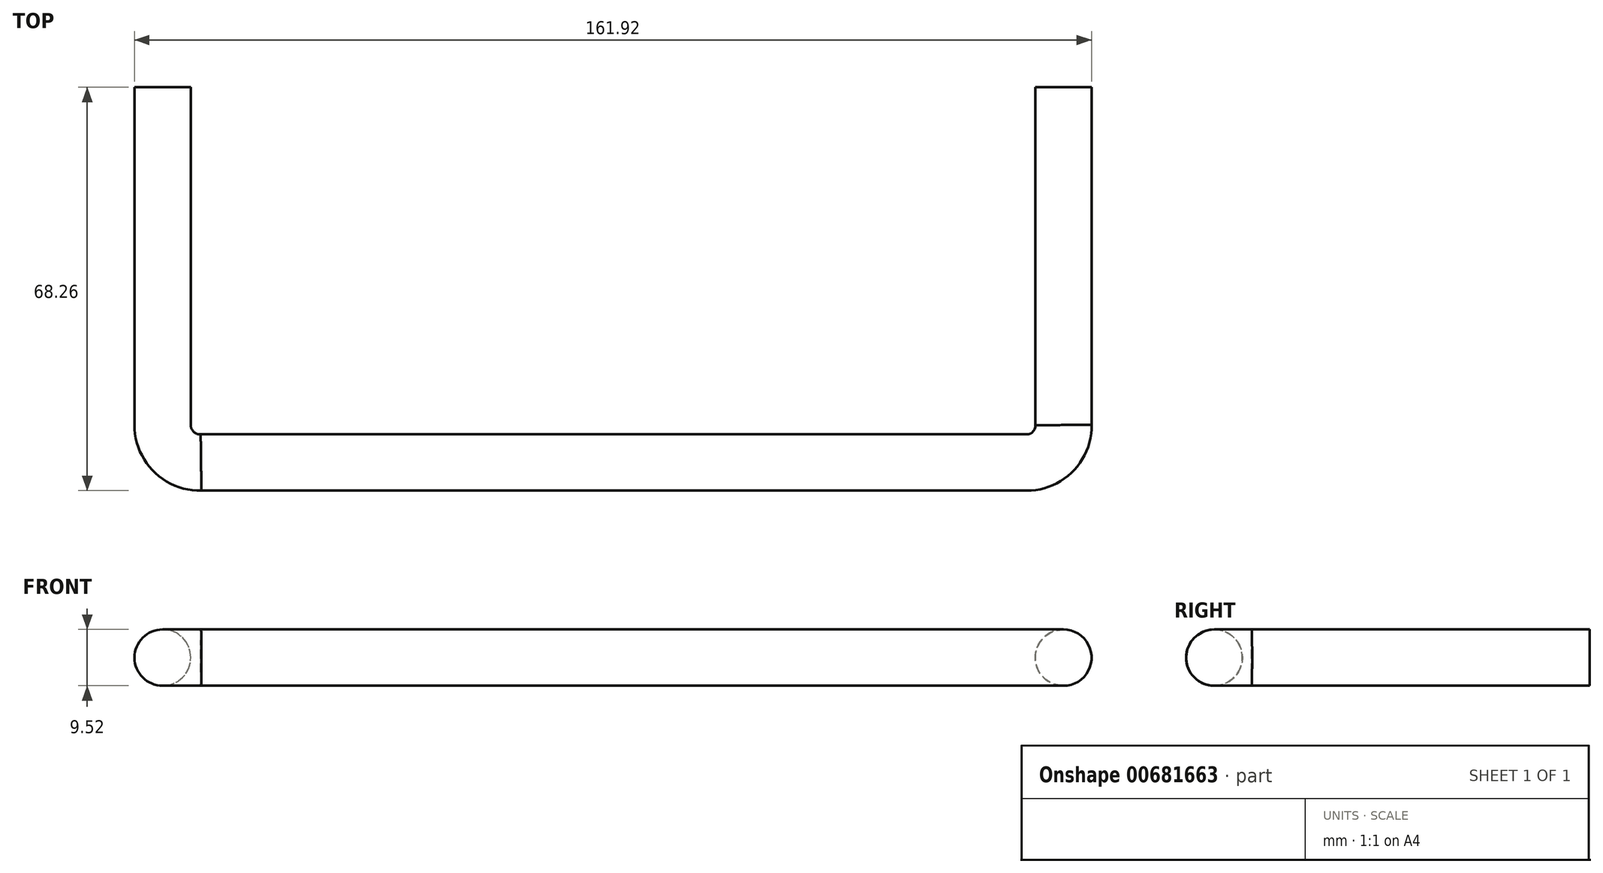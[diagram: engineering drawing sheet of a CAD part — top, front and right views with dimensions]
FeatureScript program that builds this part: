
annotation { "Feature Type Name" : "Feature", "Feature Type Description" : "" }
export const myFeature = defineFeature(function(context is Context, id is Id, definition is map)
    precondition{}
    {
        {
            var Q0;
            Q0=qCreatedBy(makeId("Front.planeOp"),FACE);
            var sketch = newSketch(context, id + "F0", { "sketchPlane" : qUnion([Q0])});
            skCircle(sketch, "E0", {"center": v(0, 0) * mm, "radius": 4.76 * mm});
            skSolve(sketch);
        }
        {
            var Q0;
            Q0=qCreatedBy(makeId("Top.planeOp"),FACE);
            var sketch = newSketch(context, id + "F1", { "sketchPlane" : qUnion([Q0])});
            skLineSegment(sketch, "E1", {"start": v(0, 0) * mm, "end": v(0, -57.15) * mm});
            skLineSegment(sketch, "E2", {"start": v(152.4, -57.15) * mm, "end": v(152.4, 0) * mm});
            skArc(sketch, "E3", {"start": v(0, -57.15) * mm, "mid": v(1.92, -61.7) * mm, "end": v(6.5, -63.5) * mm});
            skLineSegment(sketch, "E4", {"start": v(6.5, -63.5) * mm, "end": v(146.2, -63.5) * mm});
            skArc(sketch, "E5", {"start": v(146.2, -63.5) * mm, "mid": v(150.64, -61.63) * mm, "end": v(152.4, -57.15) * mm});
            skSolve(sketch);
        }
        {
            var Q0;
            Q0=makeQuery(id+"F0.imprint","IMPRINT",FACE,{"disambiguationData":[TD([[makeQuery(id+"F0.imprint","IMPRINT",EDGE,{"derivedFrom":sQuery(id+"F0.wireOp",EDGE,"E0")}),1.0]])]});
            var Q1;
            Q1=sQuery(id+"F1.wireOp",EDGE,"E1");
            var Q2;
            Q2=sQuery(id+"F1.wireOp",EDGE,"E3");
            var Q3;
            Q3=sQuery(id+"F1.wireOp",EDGE,"E4");
            var Q4;
            Q4=sQuery(id+"F1.wireOp",EDGE,"E5");
            var Q5;
            Q5=sQuery(id+"F1.wireOp",EDGE,"E2");
            sweep(context, id + "F2", {"profiles" : qUnion([Q0]), "path" : qUnion([Q1, Q2, Q3, Q4, Q5])});
        }
    });
